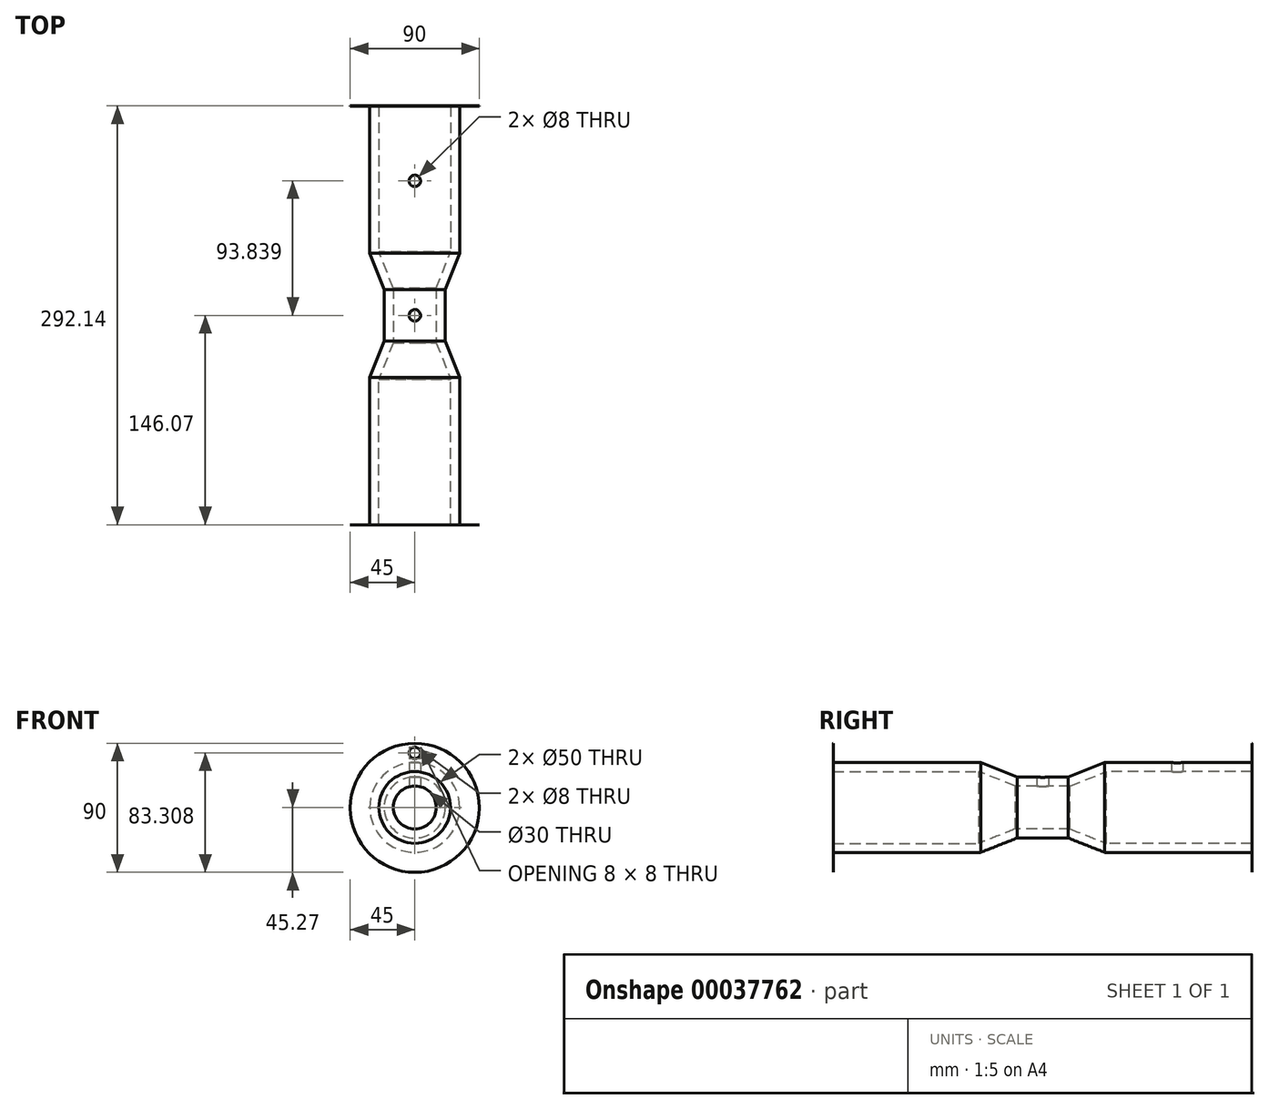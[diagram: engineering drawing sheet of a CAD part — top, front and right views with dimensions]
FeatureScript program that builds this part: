
annotation { "Feature Type Name" : "Feature", "Feature Type Description" : "" }
export const myFeature = defineFeature(function(context is Context, id is Id, definition is map)
    precondition{}
    {
        {
            var Q0;
            Q0=qCreatedBy(makeId("Right.planeOp"),FACE);
            var sketch = newSketch(context, id + "F0", { "sketchPlane" : qUnion([Q0])});
            skLineSegment(sketch, "E0", {"start": v(0, 0) * mm, "end": v(76.34, 0) * mm, "construction": true});
            skLineSegment(sketch, "E1", {"start": v(0, 15) * mm, "end": v(19.05, 15) * mm});
            skLineSegment(sketch, "E2", {"start": v(19.05, 15) * mm, "end": v(44.45, 25) * mm});
            skLineSegment(sketch, "E3", {"start": v(44.45, 25) * mm, "end": v(146.05, 25) * mm});
            skLineSegment(sketch, "E4.0", {"start": v(43.25, 31.35) * mm, "end": v(146.05, 31.35) * mm});
            skLineSegment(sketch, "E4.1", {"start": v(17.85, 21.35) * mm, "end": v(43.25, 31.35) * mm});
            skLineSegment(sketch, "E4.2", {"start": v(0, 21.35) * mm, "end": v(17.85, 21.35) * mm});
            skLineSegment(sketch, "E5", {"start": v(146.05, 31.35) * mm, "end": v(146.05, 25) * mm});
            skLineSegment(sketch, "E6", {"start": v(0, 21.35) * mm, "end": v(0, 15) * mm});
            skSolve(sketch);
        }
        {
            var Q0;
            Q0 = qSketchRegion(id + "F0", true);
            var Q1;
            Q1=sQuery(id+"F0.wireOp",EDGE,"E0");
            revolve(context, id + "F1", {"entities" : qUnion([Q0]), "axis" : qUnion([Q1]), "revolveType" : RevolveType.FULL});
        }
        {
            var Q0;
            Q0=makeQuery(id+"F1.opRevolve","SWEPT_FACE",FACE,{"disambiguationData":[OSD([sQuery(id+"F0.wireOp",EDGE,"E5")])]});
            var sketch = newSketch(context, id + "F2", { "sketchPlane" : qUnion([Q0])});
            skCircle(sketch, "E7.0", {"center": v(0, 0) * mm, "radius": 25 * mm});
            skCircle(sketch, "E8", {"center": v(0, -0.27) * mm, "radius": 45 * mm});
            skSolve(sketch);
        }
        {
            var Q0;
            Q0 = qSketchRegion(id + "F2", true);
            extrude(context, id + "F3", {"entities" : qUnion([Q0]), "operationType" : NewBodyOperationType.ADD, "depth" : 1 / 50.8 * mm});
        }
        {
            var Q0;
            Q0=makeQuery(id+"F3.opExtrude","CAP_FACE",FACE,{"disambiguationData":[OSD([sQuery(id+"F2.wireOp",EDGE,"E7.0"),sQuery(id+"F2.wireOp",EDGE,"E8")])],"isStart":false});
            var sketch = newSketch(context, id + "F4", { "sketchPlane" : qUnion([Q0])});
            skCircle(sketch, "E9.0", {"center": v(0, 0) * mm, "radius": 31.35 * mm, "construction": true});
            skLineSegment(sketch, "E10", {"start": v(0, 44.73) * mm, "end": v(0, 31.35) * mm, "construction": true});
            skPoint(sketch, "E11", {"position": v(0, 38.04) * mm});
            skSolve(sketch);
        }
        {
            var Q0;
            Q0=sQuery(id+"F4.wireOp",VERTEX,"E11");
            var Q1;
            Q1=makeQuery(id+"F1.opRevolve","SWEPT_BODY",BODY,{"disambiguationData":[OSD([sQuery(id+"F0.wireOp",EDGE,"E1"),sQuery(id+"F0.wireOp",EDGE,"E2"),sQuery(id+"F0.wireOp",EDGE,"E3"),sQuery(id+"F0.wireOp",EDGE,"E4.0"),sQuery(id+"F0.wireOp",EDGE,"E4.1"),sQuery(id+"F0.wireOp",EDGE,"E4.2"),sQuery(id+"F0.wireOp",EDGE,"E5"),sQuery(id+"F0.wireOp",EDGE,"E6")])]});
            hole(context, id + "F5", {"style" : HoleStyle.SIMPLE, "endStyle" : HoleEndStyle.THROUGH, "holeDiameter" : 8 * mm, "tappedDepth" : 12 * mm, "tapClearance" : 3, "locations" : qUnion([Q0]), "scope" : qUnion([Q1])});
        }
        {
            var Q0;
            Q0=makeQuery(id+"F1.opRevolve","SWEPT_BODY",BODY,{"disambiguationData":[OSD([sQuery(id+"F0.wireOp",EDGE,"E1"),sQuery(id+"F0.wireOp",EDGE,"E2"),sQuery(id+"F0.wireOp",EDGE,"E3"),sQuery(id+"F0.wireOp",EDGE,"E4.0"),sQuery(id+"F0.wireOp",EDGE,"E4.1"),sQuery(id+"F0.wireOp",EDGE,"E4.2"),sQuery(id+"F0.wireOp",EDGE,"E5"),sQuery(id+"F0.wireOp",EDGE,"E6")])]});
            var Q1;
            Q1=qCreatedBy(makeId("Front.planeOp"),FACE);
            mirror(context, id + "F6", {"operationType" : NewBodyOperationType.ADD, "entities" : qUnion([Q0]), "mirrorPlane" : qUnion([Q1])});
        }
        {
            var Q0;
            Q0=qCreatedBy(makeId("Top.planeOp"),FACE);
            cPlane(context, id + "F7", {"entities" : qUnion([Q0]), "cplaneType" : CPlaneType.OFFSET, "offset" : 34 * mm, "width" : 150 * mm, "height" : 150 * mm});
        }
        {
            var Q0;
            Q0=qCreatedBy(id+"F7.planeOp",FACE);
            var sketch = newSketch(context, id + "F8", { "sketchPlane" : qUnion([Q0])});
            skPoint(sketch, "E12", {"position": v(0, 0) * mm});
            skLineSegment(sketch, "E13", {"start": v(0, 0) * mm, "end": v(0, 129.82) * mm, "construction": true});
            skPoint(sketch, "E14", {"position": v(0, 93.84) * mm});
            skSolve(sketch);
        }
        {
            var Q0;
            Q0=sQuery(id+"F8.wireOp",VERTEX,"E14");
            var Q1;
            Q1=sQuery(id+"F8.wireOp",VERTEX,"E12");
            var Q2;
            Q2=makeQuery(id+"F1.opRevolve","SWEPT_BODY",BODY,{"disambiguationData":[OSD([sQuery(id+"F0.wireOp",EDGE,"E1"),sQuery(id+"F0.wireOp",EDGE,"E2"),sQuery(id+"F0.wireOp",EDGE,"E3"),sQuery(id+"F0.wireOp",EDGE,"E4.0"),sQuery(id+"F0.wireOp",EDGE,"E4.1"),sQuery(id+"F0.wireOp",EDGE,"E4.2"),sQuery(id+"F0.wireOp",EDGE,"E5"),sQuery(id+"F0.wireOp",EDGE,"E6")])]});
            hole(context, id + "F9", {"style" : HoleStyle.SIMPLE, "endStyle" : HoleEndStyle.BLIND, "holeDiameter" : 8 * mm, "holeDepth" : 12 * mm, "tappedDepth" : 12 * mm, "tapClearance" : 3, "locations" : qUnion([Q0, Q1]), "scope" : qUnion([Q2])});
        }
    });
